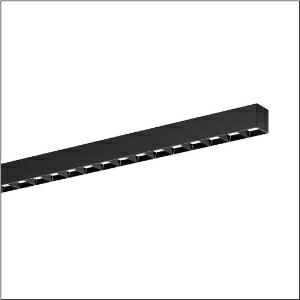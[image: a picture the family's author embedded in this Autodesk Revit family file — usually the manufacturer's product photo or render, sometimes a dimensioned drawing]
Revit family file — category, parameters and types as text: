
# Revit family: silica_r__21_51mx24dc4abb_c2b6
name_source: partatom
category: Lighting Fixtures
units: mm (PartAtom-declared; Revit-internal decimal feet)

## family parameters
Cut with Voids When Loaded = No
Host = Face
Light Source = No
Part Type = Normal
Room Calculation Point = No
Round Connector Dimension = Use Diameter
Shared = No

## types (1)
- --- (1 x LED, 10800 lm, 73.7 W, 4000K)
    Apparent Load = 74 VA
    CIE Flux Codes = 74 94 99 100 100
    Color Rendering = 80
    Color Temperature = 4000K
    Default Elevation = 1800 mm
    Description = Silica® 21, office luminaire, primary light control with darklight reflector, of PMMA, black, CAT 2 (L<= 3000cd/m²), light emission: direct distribution, primary light characteristic: asymmetric, installation type: surface-mounted, LED, rated luminous flux: 10.800lm, luminous efficacy: 147lm/W, light colour: 840, colour temperature: 4000K, with terminal, 3+2-pole, max. 2.5mm², mains connection: 220..240V, AC, 50/60Hz, rated input power: 73.7W, luminaire housing, of aluminium, jet black (RAL 9005), length: 3.004mm, width: 53mm, height: 53mm, protection rating (complete): IP20, insulation class (complete): insulation class I (protective earthing), certification: CE, permissible operating ambient temperature: 0..+35°C, standard: EN 50419, packaging unit: 1 piece
    Height = 0 mm  [stored 0 ft]
    Lamp = 1 x LED
    Lamp Light Flux = 10800 lm
    Lamp Power = 73.7 W
    Lamp count = 1
    Length = 3004 mm
    Luminous efficacy = 147 lm/W
    Manufacturer = Siteco
    ModVariant = No
    Model = 51MX24DC4ABB
    Mounting Place = Ceiling
    Mounting Type = Recessed
    Number of Poles = 1
    OnlyDefault = Yes
    Power Factor = 1
    Product Name = Silica® 21
    Product group = office luminaire | ceiling recessed
    ProductGroupID = 401
    Protection Class = Protection class I
    Protection Degree = IP 20
    RLX_Detail_Level = 1
    RLX_Emergency_Light_Flux = 0 lm
    RLX_Emergency_Type = 0
    RLX_Emergency_Type_DB = No
    RlxData = <blob elided: 64329 chars, md5=7c4a629e>
    Socket = socket
    Standby Power = 0 W
    System Light Flux = 10800 lm
    System Power = 74 W
    Type Comments = factory setting: luminous flux: 100 % | dim-lin: 254 | 418 mA
    Type Image = l_1313577.jpg
    URL = http://relux.com
    VarID = @adj_071719
    Voltage = 0 V
    Weight = 0.00 kg
    Width = 53 mm

note: [stored X ft] marks values corroborated as IEEE doubles in the binary element streams (Revit-internal decimal feet)

## geometry (parser evidence)
native form markers: Blend x4, Sweep x10
no freeform markers — native parametric forms only
